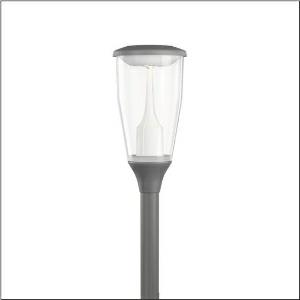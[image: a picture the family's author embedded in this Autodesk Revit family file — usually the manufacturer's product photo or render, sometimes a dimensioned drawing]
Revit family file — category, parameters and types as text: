
# Revit family: dl_11_iq___p1_0a_5xa5575nf14hp00022_d0ce
name_source: partatom
category: Lighting Fixtures
units: mm (PartAtom-declared; Revit-internal decimal feet)

## family parameters
Cut with Voids When Loaded = No
Host = Face
Light Source = No
Part Type = Normal
Room Calculation Point = No
Round Connector Dimension = Use Diameter
Shared = No

## types (1)
- --- (1 x LED, 4280 lm, 33.6 W, 2700K)
    Apparent Load = 34 VA
    CIE Flux Codes = 33 63 91 94 100
    Color Rendering = 70
    Color Temperature = 2700K
    Default Elevation = 1800 mm
    Description = DL 11 iQ, mast luminaire, Module 540 iQ-SR, primary light control with 3 zone facetted reflector, of plastic, silver coated, highly specular, structured, primary optical cover: cover, of PMMA, transparent, light distribution: P1.0a, light emission: direct distribution, primary light characteristic: asymmetric, installation type: post-top, LED, High Power LED, light colour: 727, colour temperature: 2700K, control gear: iQ Street-Remote, control: Street-Remote, Auto-Match, Temp-Guard, Lumen-Switch, Night-Set, Smart-Wire, Light-Fading, Desk-Remote (wireless, voltage-free reading and setting of iQ features in the workshop via application-optimized NFC function/RFID function), optimised constant luminous flux control (CLO 2.0), mains connection: 220..240V, AC, 50/60Hz, connection cable pre-assembled, cable length: 5,5m, wiring characteristics: H07RN-F, 5-core, 1.5mm², start of lifetime: 34W, end of service life: 36W, luminaire housing, upper part, of diecast aluminium, coated, Siteco® metallic grey (DB 702S), spigot size: 76mm (post-top), mounting height: 3..5m, post-top mast mounting element, of diecast aluminium, coated, Siteco® metallic grey (DB 702S), Module 540 iQ-SR, traffic white (RAL 9016), equipment: Power, protection rating (complete): IP66, insulation class (complete): insulation class II (safety insulation), certification: CE, ENEC, ENEC+, VDE, impact resistance: IK07, packaging unit: 1 piece

Light Distribution: P1.0a
    Height = 665 mm
    Lamp = 1 x LED
    Lamp Light Flux = 4280 lm
    Lamp Power = 33.6 W
    Lamp count = 1
    Length = 334 mm
    Luminous efficacy = 127 lm/W
    Manufacturer = Siteco
    ModVariant = No
    Model = 5XA5575NF14HP00022
    Number of Poles = 1
    OnlyDefault = Yes
    Power Factor = 1
    Product Name = DL 11 iQ | P1.0a
    Product group = mast luminaire | pylon top
    ProductGroupID = 6100
    Protection Class = Protection class II
    Protection Degree = IP 66
    RLX_Detail_Level = 1
    RLX_Emergency_Light_Flux = 0 lm
    RLX_Emergency_Type = 0
    RLX_Emergency_Type_DB = No
    RlxData = <blob elided: 105365 chars, md5=0fb4c29a>
    Socket = socket
    Standby Power = 0 W
    System Light Flux = 4280 lm
    System Power = 34 W
    Type Comments = factory setting: luminous flux: 100 % | dim-lin: 254 | 695 mA
    Type Image = l_1258354.jpg
    URL = http://relux.com
    VarID = @adj_033170
    Voltage = 0 V
    Weight = 0.00 kg
    Width = 0 mm  [stored 0 ft]

note: [stored X ft] marks values corroborated as IEEE doubles in the binary element streams (Revit-internal decimal feet)

## geometry (parser evidence)
native form markers: Blend x4, Sweep x11
no freeform markers — native parametric forms only
